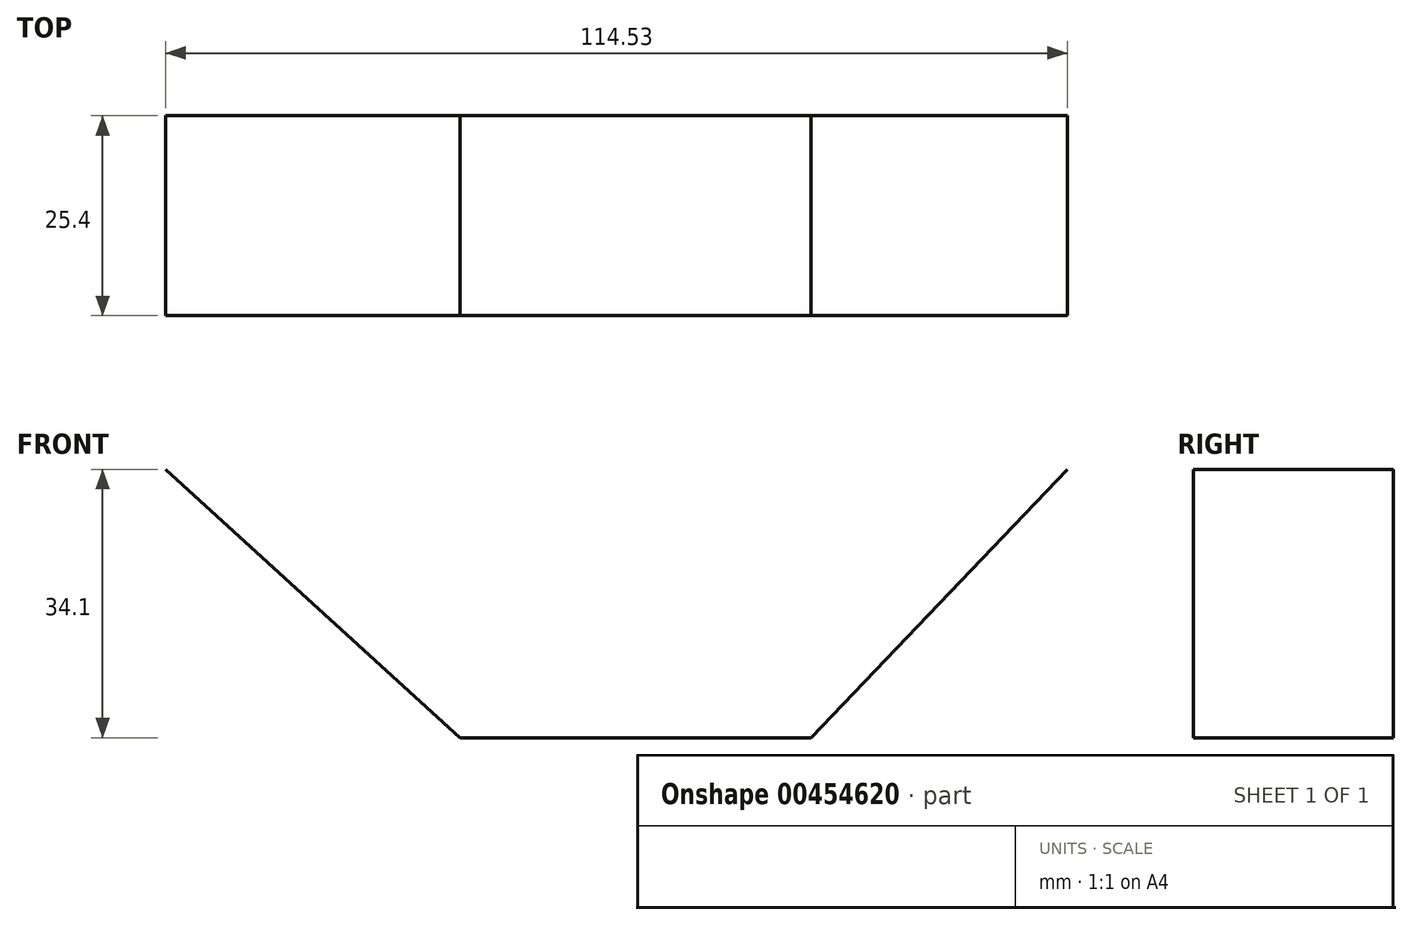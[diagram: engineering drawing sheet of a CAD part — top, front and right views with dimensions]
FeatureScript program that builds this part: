
annotation { "Feature Type Name" : "Feature", "Feature Type Description" : "" }
export const myFeature = defineFeature(function(context is Context, id is Id, definition is map)
    precondition{}
    {
        {
            var Q0;
            Q0=qCreatedBy(makeId("Front.planeOp"),FACE);
            var sketch = newSketch(context, id + "F0", { "sketchPlane" : qUnion([Q0])});
            skLineSegment(sketch, "E0", {"start": v(-18.7, 0) * mm, "end": v(25.85, 0) * mm});
            skLineSegment(sketch, "E1", {"start": v(25.85, 0) * mm, "end": v(58.44, 34.1) * mm});
            skLineSegment(sketch, "E2", {"start": v(58.44, 34.1) * mm, "end": v(-56.1, 34.1) * mm});
            skLineSegment(sketch, "E3", {"start": v(-56.1, 34.1) * mm, "end": v(-18.7, 0) * mm});
            skSolve(sketch);
        }
        {
            var Q0;
            Q0=sQuery(id+"F0.wireOp",EDGE,"E0");
            var Q1;
            Q1=sQuery(id+"F0.wireOp",EDGE,"E1");
            var Q2;
            Q2=sQuery(id+"F0.wireOp",EDGE,"E3");
            extrude(context, id + "F1", {"bodyType" : ToolBodyType.SURFACE, "surfaceEntities" : qUnion([Q0, Q1, Q2]), "depth" : 25.4 * mm, "offsetDistance" : 25.4 * mm});
        }
    });
